# Revit family: Haworth_Masters_Wardrobe_Tower
name_source: partatom
category: Furniture Systems
revit_build: Autodesk Revit 2018 (Build: 20170223_1515(x64)
units: mm (PartAtom-declared; Revit-internal decimal feet)

## family parameters
Always vertical = Yes
Cut with Voids When Loaded = No
OmniClass Number = 23.40.70.14.64.21
OmniClass Title = Systems Furniture
Part Type = Normal
Room Calculation Point = No
Round Connector Dimension = Use Diameter
Shared = No
Work Plane-Based = No

## types (2) — shared parameters
Actual Depth = 18"
Actual Height = 49"
Actual Width = 12"
Assembly Code = E2020200
Bar Pull = No
Base Height = 3"
Classic Pull = Yes
Description = Haworth - Masters - Wardrobe Tower
Door Height = 46"
Door Pull Offset = 1 1/2"
Door Width = 11 7/8"
Linear Pull = No
Manufacturer = Haworth
Max. Height = 81 5/8"
Max. Width = 36"
Min. Height = 69"
Min. Width = 30"
Model = Haworth - Masters - Wardrobe Tower
Panel Thickness = 3/4"
Pull Finish = Haworth _ Metal _ Brushed Aluminum
Pull Height Centerline = 33"
Pull Offset Centerline = 3"
Revision Number = 3
Size = Verify Final Dim. w/ Haworth
Sustainability Info = http://www.haworth.com
Touch Latch = No
URL = www.haworth.com
URL - Product = http://www.haworth.com
Warranty = http://www.haworth.com

## per-type parameters (varying)
| type | Cabinet Finish | Door Finish |
| Five High | Haworth _ Wood _ Undecided | Haworth _ Wood _ Undecided |
| Six High | Haworth _ Wood _ White Oak | Haworth _ Wood _ White Oak |

## geometry (parser evidence)
native form markers: Sweep x7
no freeform markers — native parametric forms only
